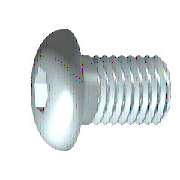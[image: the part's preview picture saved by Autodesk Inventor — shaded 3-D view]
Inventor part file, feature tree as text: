
AUTODESK INVENTOR PART (.ipt)
format: ipt  version: 2015 (Build 190159000, 159)  size: 190,464 bytes
history: native  units: mm (DEFAULTED — no unit token found)
features: sketch x2, extrude x1, plane x1, fillet x1
ambient origin geometry x7: Origin, YZ Plane, XY Plane, X Axis, Y Axis, Z Axis, Center Point
bodies: Solid1 (feature_tree), Body (feature_tree)
feature tree (5):
  extrude  "Slot"  Depth=1.8542mm
  plane  "Work Plane1"
  fillet  "Fillet2"  Radius=1.8542mm
  sketch  "Sketch1"  dims[d1=17.45976mm d2=1.59014mm d3=1.8542mm]
  sketch  "Sketch2"  dims[d4=1.1176mm d5=60.0deg d6=3.5052mm d7=3.5052mm d8=2.287693mm d9=6.6548mm d10=90.0deg d11=10.0mm d12=0.0mm d13=17.45976mm d14=0.0mm d15=0.486918mm d16=0.486918mm d17=1.6002mm d19=0.0mm d26=19.05mm d27=45.0deg d28=0.0mm d29=0.0mm d30=0.1mm]
